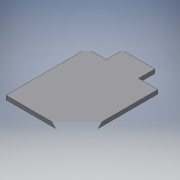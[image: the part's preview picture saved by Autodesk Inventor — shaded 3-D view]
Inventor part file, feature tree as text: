
AUTODESK INVENTOR PART (.ipt)
format: ipt  version: 2016 (Build 200138000, 138)  size: 121,856 bytes
history: native  units: in
note: dims shown in document units (in); Inventor stores cm internally (conversion verified against a paired STEP export)
features: extrude x4, sketch x4, projected_geometry x1
ambient origin geometry x8: Origin, YZ Plane, XZ Plane, XY Plane, X Axis, Y Axis, Z Axis, Center Point
bodies: Solid1 (feature_tree)
feature tree (9):
  extrude  "Extrusion1"  Depth=0.0197in
  extrude  "Extrusion2"  Depth=0.1575in
  extrude  "Extrusion3"  Depth=0.0197in TaperAngle=0.0deg
  extrude  "Extrusion4"  Depth=0.0394in TaperAngle=0.0deg
  sketch  "Sketch1"  dims[d0=0.0197in d1=0.5906in]
  sketch  "Sketch2"  dims[d2=0.3937in d3=0.0in d4=0.1575in]
  sketch  "Sketch3"  dims[d5=0.0787in d6=0.0197in d7=0.0in]
  projected_geometry  "Projected Loop1"
  sketch  "Sketch4"  dims[d8=0.0394in d9=0.0in d10=0.0394in d11=0.0in]
